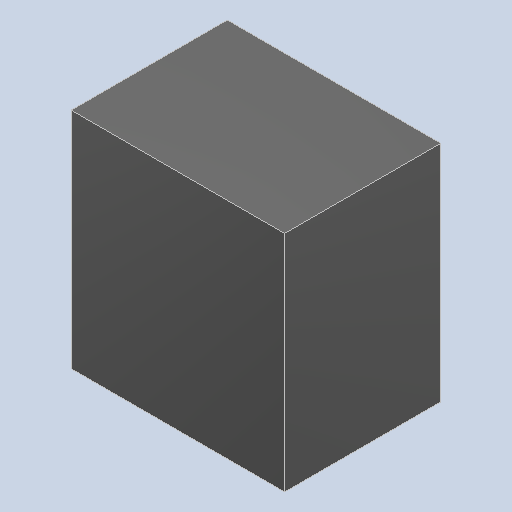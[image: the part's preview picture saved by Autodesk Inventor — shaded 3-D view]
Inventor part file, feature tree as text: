
AUTODESK INVENTOR PART (.ipt)
format: ipt  version: 2023.4 (Build 274418000, 418)  size: 83,968 bytes
history: native  units: mm
features: extrude x1
ambient origin geometry x8: Origin, YZ Plane, XZ Plane, XY Plane, X Axis, Y Axis, Z Axis, Center Point
bodies: Solid1 (feature_tree)
feature tree (1):
  extrude  "Extruded"  [1 undecoded]
note: 1 required parameter value undecoded (feature->parameter linkage not recoverable at this tier; creation-order binding heuristic only, values carry confidence <= 0.55)
